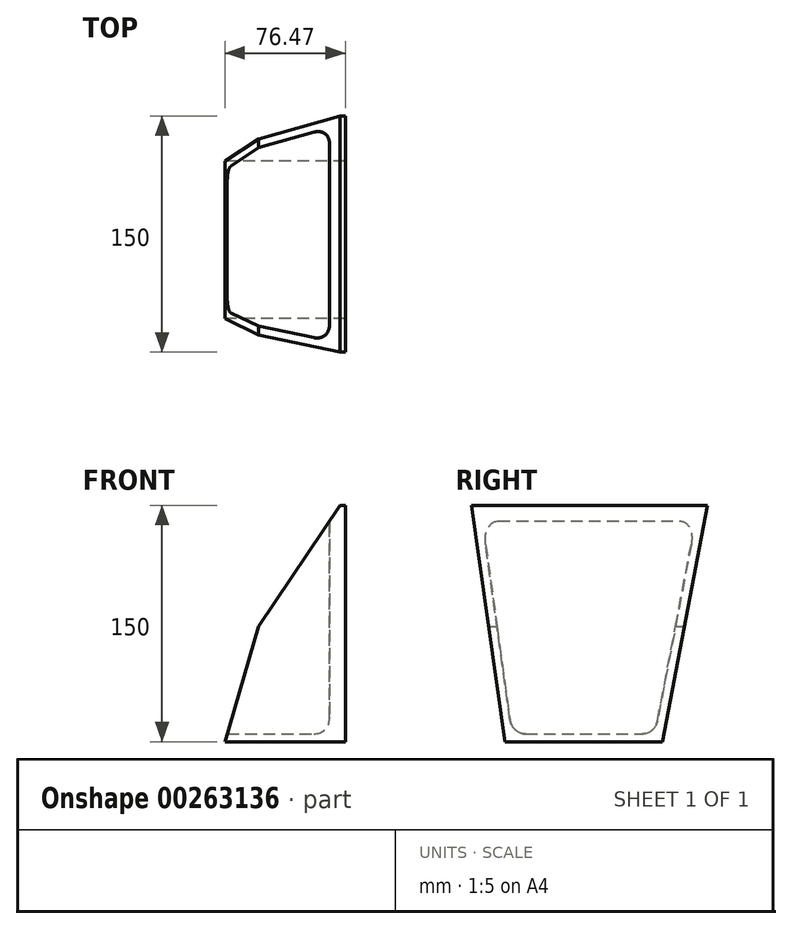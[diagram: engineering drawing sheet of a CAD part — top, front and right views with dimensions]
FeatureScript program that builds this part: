
annotation { "Feature Type Name" : "Feature", "Feature Type Description" : "" }
export const myFeature = defineFeature(function(context is Context, id is Id, definition is map)
    precondition{}
    {
        {
            var Q0;
            Q0=qCreatedBy(makeId("Right.planeOp"),FACE);
            var sketch = newSketch(context, id + "F0", { "sketchPlane" : qUnion([Q0])});
            skLineSegment(sketch, "E0", {"start": v(-65.8, 102.41) * mm, "end": v(84.2, 102.41) * mm});
            skLineSegment(sketch, "E1", {"start": v(-44.48, -47.59) * mm, "end": v(55.52, -47.59) * mm});
            skLineSegment(sketch, "E2", {"start": v(55.52, -47.59) * mm, "end": v(84.2, 102.41) * mm});
            skLineSegment(sketch, "E3", {"start": v(-65.8, 102.41) * mm, "end": v(-44.48, -47.59) * mm});
            skLineSegment(sketch, "E4", {"start": v(55.52, -47.59) * mm, "end": v(-44.48, -47.59) * mm});
            skSolve(sketch);
        }
        {
            var Q0;
            Q0=makeQuery(id+"F0.imprint","IMPRINT",FACE,{"disambiguationData":[TD([[makeQuery(id+"F0.imprint","IMPRINT",EDGE,{"derivedFrom":sQuery(id+"F0.wireOp",EDGE,"E2")}),1.0]])]});
            extrude(context, id + "F1", {"entities" : qUnion([Q0]), "depth" : 100 * mm});
        }
        {
            var Q0;
            Q0=makeQuery(id+"F1.opExtrude","CAP_FACE",FACE,{"disambiguationData":[OSD([sQuery(id+"F0.wireOp",EDGE,"E2"),sQuery(id+"F0.wireOp",EDGE,"E3"),sQuery(id+"F0.wireOp",EDGE,"E0"),sQuery(id+"F0.wireOp",EDGE,"E4")])],"isStart":true});
            var sketch = newSketch(context, id + "F2", { "sketchPlane" : qUnion([Q0])});
            skLineSegment(sketch, "E5", {"start": v(-78.62, 102.41) * mm, "end": v(-50.9, -42.58) * mm});
            skLineSegment(sketch, "E6", {"start": v(-50.9, -42.58) * mm, "end": v(39.92, -42.71) * mm});
            skLineSegment(sketch, "E7", {"start": v(39.92, -42.71) * mm, "end": v(60.1, 102.41) * mm});
            skLineSegment(sketch, "E8", {"start": v(-78.62, 102.41) * mm, "end": v(60.1, 102.41) * mm});
            skSolve(sketch);
        }
        {
            var Q0;
            Q0 = qSketchRegion(id + "F2", true);
            extrude(context, id + "F3", {"entities" : qUnion([Q0]), "operationType" : NewBodyOperationType.REMOVE, "oppositeDirection" : true, "depth" : 90 * mm});
        }
        {
            var Q0;
            Q0=makeQuery(id+"F3.boolean.opBoolean","COPY",EDGE,{"derivedFrom":makeQuery(id+"F3.opExtrude","SWEPT_EDGE",EDGE,{"disambiguationData":[OSD([sQuery(id+"F2.wireOp",EDGE,"E5"),sQuery(id+"F2.wireOp",EDGE,"E6")])]})});
            var Q1;
            Q1=makeQuery(id+"F3.boolean.opBoolean","COPY",EDGE,{"derivedFrom":makeQuery(id+"F3.opExtrude","CAP_EDGE",EDGE,{"disambiguationData":[OSD([sQuery(id+"F2.wireOp",EDGE,"E6")])],"isStart":false})});
            var Q2;
            Q2=makeQuery(id+"F3.boolean.opBoolean","COPY",EDGE,{"derivedFrom":makeQuery(id+"F3.opExtrude","SWEPT_EDGE",EDGE,{"disambiguationData":[OSD([sQuery(id+"F2.wireOp",EDGE,"E6"),sQuery(id+"F2.wireOp",EDGE,"E7")])]})});
            var Q3;
            Q3=makeQuery(id+"F3.boolean.opBoolean","COPY",EDGE,{"derivedFrom":makeQuery(id+"F3.opExtrude","CAP_EDGE",EDGE,{"disambiguationData":[OSD([sQuery(id+"F2.wireOp",EDGE,"E5")])],"isStart":false})});
            var Q4;
            Q4=makeQuery(id+"F3.boolean.opBoolean","COPY",EDGE,{"derivedFrom":makeQuery(id+"F3.opExtrude","CAP_EDGE",EDGE,{"disambiguationData":[OSD([sQuery(id+"F2.wireOp",EDGE,"E7")])],"isStart":false})});
            fillet(context, id + "F4", {"entities" : qUnion([Q0, Q1, Q2, Q3, Q4]), "radius" : 10 * mm, "tangentPropagation" : true, "allowEdgeOverflow" : false});
        }
        {
            var Q0;
            Q0=qCreatedBy(makeId("Front.planeOp"),FACE);
            var sketch = newSketch(context, id + "F5", { "sketchPlane" : qUnion([Q0])});
            skLineSegment(sketch, "E9", {"start": v(18.05, -66.48) * mm, "end": v(44.83, 25.72) * mm});
            skLineSegment(sketch, "E10", {"start": v(44.83, 25.72) * mm, "end": v(101.29, 109.24) * mm});
            skLineSegment(sketch, "E11", {"start": v(18.05, -66.48) * mm, "end": v(-27.02, -66.48) * mm});
            skLineSegment(sketch, "E12", {"start": v(-27.02, -66.48) * mm, "end": v(-27.02, 105.97) * mm});
            skLineSegment(sketch, "E13", {"start": v(-27.02, 105.97) * mm, "end": v(101.29, 109.24) * mm});
            skSolve(sketch);
        }
        {
            var Q0;
            Q0 = qSketchRegion(id + "F5", true);
            extrude(context, id + "F6", {"entities" : qUnion([Q0]), "operationType" : NewBodyOperationType.REMOVE, "endBound" : BoundingType.THROUGH_ALL, "depth" : 25 * mm, "hasSecondDirection" : true, "secondDirectionBound" : SecondDirectionBoundingType.THROUGH_ALL, "secondDirectionOppositeDirection" : true, "secondDirectionDepth" : 25 * mm});
        }
    });
